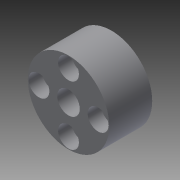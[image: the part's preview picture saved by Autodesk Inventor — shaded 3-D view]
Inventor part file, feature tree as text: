
AUTODESK INVENTOR PART (.ipt)
format: ipt  version: 2015 (Build 190159000, 159)  size: 115,712 bytes
history: native  units: in
note: dims shown in document units (in); Inventor stores cm internally (conversion verified against a paired STEP export)
features: extrude x2, sketch x2, projected_geometry x1
ambient origin geometry x8: Origin, YZ Plane, XZ Plane, XY Plane, X Axis, Y Axis, Z Axis, Center Point
bodies: Solid1 (feature_tree)
feature tree (5):
  extrude  "Extrusion1"  Depth=0.3125in
  extrude  "Extrusion6"  [1 undecoded]
  sketch  "Sketch1"  dims[d0=0.3125in d1=0.0in d12=0.222in]
  sketch  "Sketch6"  dims[d13=0.145in d14=0.0in]
  projected_geometry  "Projected Loop1"
note: 1 required parameter value undecoded (feature->parameter linkage not recoverable at this tier; creation-order binding heuristic only, values carry confidence <= 0.55)
